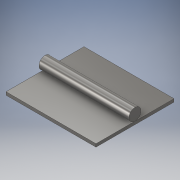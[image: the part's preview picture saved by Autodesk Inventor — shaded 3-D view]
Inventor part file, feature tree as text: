
AUTODESK INVENTOR PART (.ipt)
format: ipt  version: 2019 (Build 230136000, 136)  size: 115,712 bytes
history: native  units: mm
features: extrude x1, sketch x1
ambient origin geometry x8: Origin, YZ Plane, XZ Plane, XY Plane, X Axis, Y Axis, Z Axis, Center Point
bodies: Solid1 (feature_tree)
feature tree (2):
  extrude  "Extrusion1"  Depth=13.0mm
  sketch  "Sketch1"  dims[d0=0.5mm d1=13.0mm d2=2.0mm d3=15.0mm d4=0.0mm]
